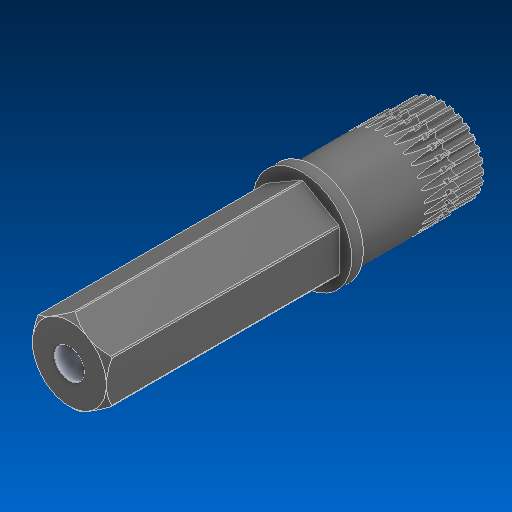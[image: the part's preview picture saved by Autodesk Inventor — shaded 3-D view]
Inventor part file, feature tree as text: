
AUTODESK INVENTOR PART (.ipt)
format: ipt  version: 2022.2 (Build 262287000, 287)  size: 1,428,992 bytes
history: native  units: in
note: dims shown in document units (in); Inventor stores cm internally (conversion verified against a paired STEP export)
features: fillet x1
ambient origin geometry x8: Origin, YZ Plane, XZ Plane, XY Plane, X Axis, Y Axis, Z Axis, Center Point
bodies: Solid1 (feature_tree)
feature tree (1):
  fillet  "Fillet5"  [1 undecoded]
note: 1 required parameter value undecoded (feature->parameter linkage not recoverable at this tier; creation-order binding heuristic only, values carry confidence <= 0.55)
